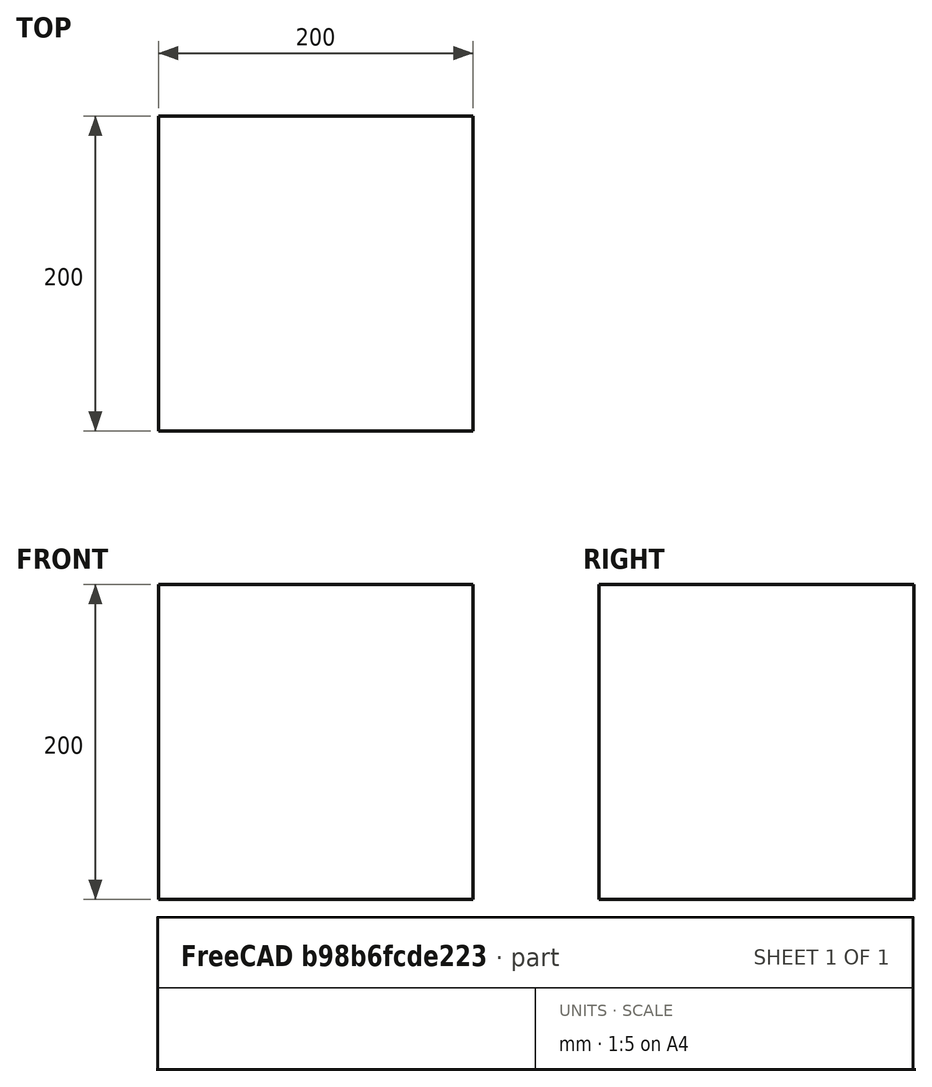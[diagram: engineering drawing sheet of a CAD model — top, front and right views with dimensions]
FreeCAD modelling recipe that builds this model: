
FCSTD DOCUMENT  (FreeCAD 0.17R13541 (Git))
Label: helloworld
License: All rights reserved
LicenseURL: http://en.wikipedia.org/wiki/All_rights_reserved
objects: Sketcher::SketchObject×1, PartDesign::Pad×1, PartDesign::Body×1
note: 4 computed .brp shape members not serialized (recipe doc carries the construction recipe); baked Part::Feature solids carry a one-line shape summary decoded from their .brp

FEATURE [Sketcher::SketchObject] Sketch
  MapMode = 5
  Support = -> [XY_Plane]
  sketch-geometry (4):
    g0: LineSegment StartX=-100 StartY=100 StartZ=0 EndX=100 EndY=100 EndZ=0
    g1: LineSegment StartX=100 StartY=100 StartZ=0 EndX=100 EndY=-100 EndZ=0
    g2: LineSegment StartX=100 StartY=-100 StartZ=0 EndX=-100 EndY=-100 EndZ=0
    g3: LineSegment StartX=-100 StartY=-100 StartZ=0 EndX=-100 EndY=100 EndZ=0
  constraints (12):
    c: Coincident(g0,g1)
    c: Coincident(g1,g2)
    c: Coincident(g2,g3)
    c: Coincident(g3,g0)
    c: Horizontal(g0)
    c: Horizontal(g2)
    c: Vertical(g1)
    c: Vertical(g3)
    c: Symmetric(g0,g2,g-1)
    c: Symmetric(g0,g0,g-2)
    c: Equal(g0,g1)
    c: DistanceX(g0,g0) = 200
FEATURE [PartDesign::Pad] Pad
  Length = 200
  Length2 = 100
  Midplane = true
  Profile = -> Sketch
  Type = 0
FEATURE [PartDesign::Body] Body
  Group = -> [Sketch,Pad]
  Origin = -> Origin
  Tip = -> Pad
